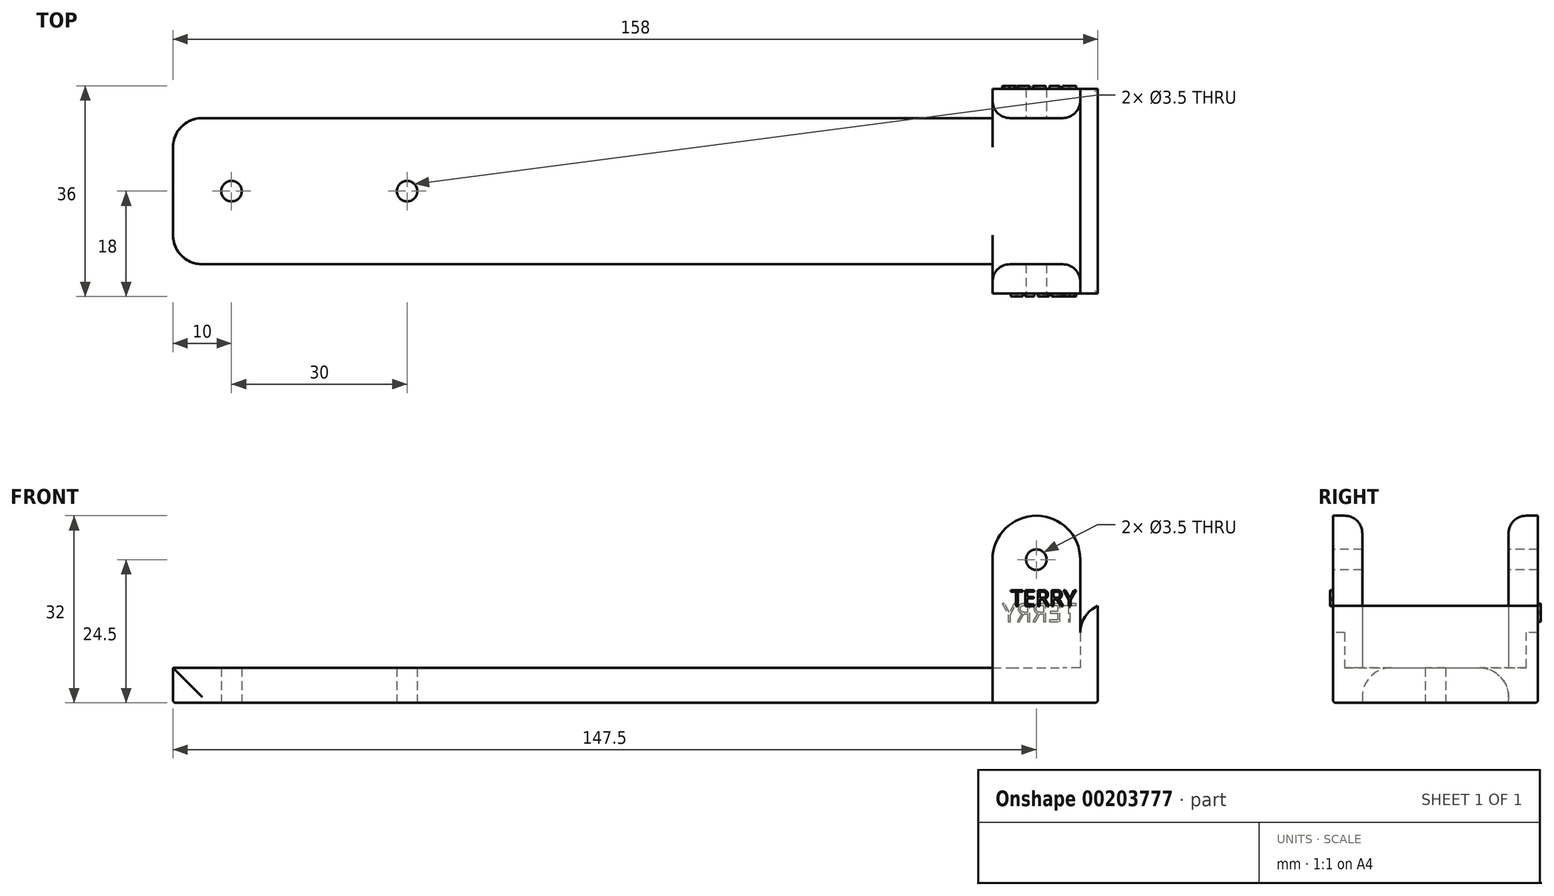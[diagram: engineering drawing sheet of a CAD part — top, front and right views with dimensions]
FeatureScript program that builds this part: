
annotation { "Feature Type Name" : "Feature", "Feature Type Description" : "" }
export const myFeature = defineFeature(function(context is Context, id is Id, definition is map)
    precondition{}
    {
        {
            var Q0;
            Q0=qCreatedBy(makeId("Top.planeOp"),FACE);
            var sketch = newSketch(context, id + "F0", { "sketchPlane" : qUnion([Q0])});
            skLineSegment(sketch, "E0.bottom", {"start": v(-77.5, -12.5) * mm, "end": v(77.5, -12.5) * mm});
            skLineSegment(sketch, "E0.top", {"start": v(-77.5, 12.5) * mm, "end": v(77.5, 12.5) * mm});
            skLineSegment(sketch, "E0.left", {"start": v(-77.5, -12.5) * mm, "end": v(-77.5, 12.5) * mm});
            skLineSegment(sketch, "E0.right", {"start": v(77.5, -12.5) * mm, "end": v(77.5, 12.5) * mm});
            skPoint(sketch, "E0.middle", {"position": v(0, 0) * mm});
            skLineSegment(sketch, "E1", {"start": v(-77.5, 0) * mm, "end": v(-67.5, 0) * mm, "construction": true});
            skPoint(sketch, "E1.endSnap0", {"position": v(-77.5, 0) * mm});
            skLineSegment(sketch, "E2", {"start": v(-67.5, 0) * mm, "end": v(-37.5, 0) * mm, "construction": true});
            skCircle(sketch, "E3", {"center": v(-67.5, 0) * mm, "radius": 1.75 * mm});
            skCircle(sketch, "E4", {"center": v(-37.5, 0) * mm, "radius": 1.75 * mm});
            skSolve(sketch);
        }
        {
            var Q0;
            Q0=makeQuery(id+"F0.imprint","IMPRINT",FACE,{"disambiguationData":[TD([[makeQuery(id+"F0.imprint","IMPRINT",EDGE,{"derivedFrom":sQuery(id+"F0.wireOp",EDGE,"E0.bottom")}),1.0]])]});
            extrude(context, id + "F1", {"entities" : qUnion([Q0]), "depth" : 6 * mm});
        }
        {
            var Q0;
            Q0=qCreatedBy(makeId("Top.planeOp"),FACE);
            var sketch = newSketch(context, id + "F2", { "sketchPlane" : qUnion([Q0])});
            skLineSegment(sketch, "E5", {"start": v(0, 0) * mm, "end": v(0, -17.5) * mm, "construction": true});
            skLineSegment(sketch, "E6", {"start": v(0, -17.5) * mm, "end": v(77.5, -17.5) * mm, "construction": true});
            skLineSegment(sketch, "E7", {"start": v(77.5, -17.5) * mm, "end": v(77.5, -12.5) * mm});
            skLineSegment(sketch, "E8", {"start": v(77.5, -12.5) * mm, "end": v(62.5, -12.5) * mm});
            skLineSegment(sketch, "E9", {"start": v(62.5, -12.5) * mm, "end": v(62.5, -17.5) * mm});
            skLineSegment(sketch, "E10", {"start": v(62.5, -17.5) * mm, "end": v(77.5, -17.5) * mm});
            skLineSegment(sketch, "E11.MirrorCS", {"start": v(62.5, 17.5) * mm, "end": v(77.5, 17.5) * mm});
            skLineSegment(sketch, "E12.MirrorCS", {"start": v(62.5, 12.5) * mm, "end": v(62.5, 17.5) * mm});
            skLineSegment(sketch, "E13.MirrorCS", {"start": v(77.5, 12.5) * mm, "end": v(62.5, 12.5) * mm});
            skLineSegment(sketch, "E14.MirrorCS", {"start": v(77.5, 17.5) * mm, "end": v(77.5, 12.5) * mm});
            skSolve(sketch);
        }
        {
            var Q0;
            Q0=makeQuery(id+"F2.imprint","IMPRINT",FACE,{"disambiguationData":[TD([[makeQuery(id+"F2.imprint","IMPRINT",EDGE,{"derivedFrom":sQuery(id+"F2.wireOp",EDGE,"E11.MirrorCS")}),-1.0]])]});
            var Q1;
            Q1=makeQuery(id+"F2.imprint","IMPRINT",FACE,{"disambiguationData":[TD([[makeQuery(id+"F2.imprint","IMPRINT",EDGE,{"derivedFrom":sQuery(id+"F2.wireOp",EDGE,"E7")}),1.0]])]});
            extrude(context, id + "F3", {"entities" : qUnion([Q0, Q1]), "operationType" : NewBodyOperationType.ADD, "depth" : 32 * mm});
        }
        {
            var Q0;
            Q0=makeQuery(id+"F3.opExtrude","SWEPT_FACE",FACE,{"disambiguationData":[OSD([sQuery(id+"F2.wireOp",EDGE,"E10")])]});
            var sketch = newSketch(context, id + "F4", { "sketchPlane" : qUnion([Q0])});
            skLineSegment(sketch, "E15", {"start": v(70, 32) * mm, "end": v(70, 24.5) * mm, "construction": true});
            skCircle(sketch, "E16", {"center": v(70, 24.5) * mm, "radius": 1.75 * mm});
            skArc(sketch, "E17", {"start": v(77.5, 24.5) * mm, "mid": v(70, 32) * mm, "end": v(62.5, 24.5) * mm});
            skLineSegment(sketch, "E18", {"start": v(70, 24.5) * mm, "end": v(46.38, 24.5) * mm, "construction": true});
            skLineSegment(sketch, "E19", {"start": v(70, 24.5) * mm, "end": v(96.72, 24.5) * mm, "construction": true});
            skLineSegment(sketch, "E20", {"start": v(62.5, 24.5) * mm, "end": v(62.5, 32) * mm});
            skLineSegment(sketch, "E21", {"start": v(62.5, 32) * mm, "end": v(70, 32) * mm});
            skLineSegment(sketch, "E22", {"start": v(77.5, 32) * mm, "end": v(77.5, 24.5) * mm});
            skSolve(sketch);
        }
        {
            var Q0;
            Q0=makeQuery(id+"F4.imprint","IMPRINT",FACE,{"disambiguationData":[TD([[makeQuery(id+"F4.imprint","IMPRINT",EDGE,{"derivedFrom":sQuery(id+"F4.wireOp",EDGE,"E16")}),1.0]])]});
            var Q1;
            {var subQ0=sQuery(id+"F4.wireOp",EDGE,"E20");Q1=makeQuery(id+"F4.imprint","IMPRINT",FACE,{"disambiguationData":[TD([[makeQuery(id+"F4.imprint","IMPRINT",EDGE,{"derivedFrom":subQ0}),1.0]])]});}
            var Q2;
            {var subQ0=sQuery(id+"F4.wireOp",EDGE,"E22");Q2=makeQuery(id+"F4.imprint","IMPRINT",FACE,{"disambiguationData":[TD([[makeQuery(id+"F4.imprint","IMPRINT",EDGE,{"derivedFrom":subQ0}),-1.0]])]});}
            extrude(context, id + "F5", {"entities" : qUnion([Q0, Q1, Q2]), "operationType" : NewBodyOperationType.REMOVE, "endBound" : BoundingType.THROUGH_ALL, "oppositeDirection" : true, "depth" : 25 * mm});
        }
        {
            var Q0;
            Q0=makeQuery(id+"F3.boolean.opBoolean","MERGE",FACE,{"derivedFrom":[makeQuery(id+"F1.opExtrude","SWEPT_FACE",FACE,{"disambiguationData":[OSD([sQuery(id+"F0.wireOp",EDGE,"E0.right")])]}),makeQuery(id+"F3.opExtrude","SWEPT_FACE",FACE,{"disambiguationData":[OSD([sQuery(id+"F2.wireOp",EDGE,"E7")])]}),makeQuery(id+"F3.opExtrude","SWEPT_FACE",FACE,{"disambiguationData":[OSD([sQuery(id+"F2.wireOp",EDGE,"E14.MirrorCS")])]})]});
            var sketch = newSketch(context, id + "F6", { "sketchPlane" : qUnion([Q0])});
            skLineSegment(sketch, "E23", {"start": v(-17.5, 0) * mm, "end": v(17.5, 0) * mm});
            skLineSegment(sketch, "E24", {"start": v(17.5, 0) * mm, "end": v(17.5, 17) * mm});
            skLineSegment(sketch, "E25", {"start": v(17.5, 17) * mm, "end": v(-17.5, 17) * mm});
            skLineSegment(sketch, "E26", {"start": v(-17.5, 17) * mm, "end": v(-17.5, 0) * mm});
            skSolve(sketch);
        }
        {
            var Q0;
            Q0=makeQuery(id+"F6.imprint","IMPRINT",FACE,{"disambiguationData":[TD([[makeQuery(id+"F6.imprint","IMPRINT",EDGE,{"derivedFrom":sQuery(id+"F6.wireOp",EDGE,"E23")}),1.0]])]});
            var Q1;
            {var subQ5=makeQuery(id+"F1.opExtrude","CAP_EDGE",EDGE,{"disambiguationData":[OSD([sQuery(id+"F0.wireOp",EDGE,"E0.right")])],"isStart":false});Q1=makeQuery(id+"F6.imprint","IMPRINT",FACE,{"disambiguationData":[TD([[makeQuery(id+"F6.imprint","IMPRINT",EDGE,{"derivedFrom":subQ5}),1.0]])]});}
            extrude(context, id + "F7", {"entities" : qUnion([Q0, Q1]), "operationType" : NewBodyOperationType.ADD, "depth" : 3 * mm});
        }
        {
            var Q0;
            Q0=makeQuery(id+"F1.opExtrude","SWEPT_EDGE",EDGE,{"disambiguationData":[OSD([sQuery(id+"F0.wireOp",EDGE,"E0.top"),sQuery(id+"F0.wireOp",EDGE,"E0.left")])]});
            var Q1;
            Q1=makeQuery(id+"F1.opExtrude","SWEPT_EDGE",EDGE,{"disambiguationData":[OSD([sQuery(id+"F0.wireOp",EDGE,"E0.bottom"),sQuery(id+"F0.wireOp",EDGE,"E0.left")])]});
            var Q2;
            {var subQ0=sQuery(id+"F0.wireOp",EDGE,"E0.right");var subQ1=sQuery(id+"F0.wireOp",EDGE,"E0.bottom");Q2=makeQuery(id+"F3.boolean.opBoolean","SPLIT",EDGE,{"disambiguationData":[TD([makeQuery(id+"F1.opExtrude","SWEPT_FACE",FACE,{"disambiguationData":[OSD([subQ0])]})])],"derivedFrom":makeQuery(id+"F1.opExtrude","CAP_EDGE",EDGE,{"disambiguationData":[OSD([subQ1])],"isStart":false})});}
            var Q3;
            {var subQ0=sQuery(id+"F0.wireOp",EDGE,"E0.right");var subQ1=sQuery(id+"F0.wireOp",EDGE,"E0.top");Q3=makeQuery(id+"F3.boolean.opBoolean","SPLIT",EDGE,{"disambiguationData":[TD([makeQuery(id+"F1.opExtrude","SWEPT_FACE",FACE,{"disambiguationData":[OSD([subQ0])]})])],"derivedFrom":makeQuery(id+"F1.opExtrude","CAP_EDGE",EDGE,{"disambiguationData":[OSD([subQ1])],"isStart":false})});}
            var Q4;
            Q4=makeQuery(id+"F1.opExtrude","CAP_EDGE",EDGE,{"disambiguationData":[OSD([sQuery(id+"F0.wireOp",EDGE,"E0.right")])],"isStart":false});
            var Q5;
            {var subQ0=sQuery(id+"F6.wireOp",EDGE,"E26");var subQ1=sQuery(id+"F6.wireOp",EDGE,"E25");Q5=makeQuery(id+"F7.boolean.opBoolean","SPLIT",EDGE,{"disambiguationData":[TD([makeQuery(id+"F1.opExtrude","SWEPT_FACE",FACE,{"disambiguationData":[OSD([sQuery(id+"F0.wireOp",EDGE,"E0.right")])]}),makeQuery(id+"F3.opExtrude","SWEPT_FACE",FACE,{"disambiguationData":[OSD([sQuery(id+"F2.wireOp",EDGE,"E7")])]}),makeQuery(id+"F3.opExtrude","SWEPT_FACE",FACE,{"disambiguationData":[OSD([sQuery(id+"F2.wireOp",EDGE,"E8")])]}),makeQuery(id+"F3.opExtrude","SWEPT_FACE",FACE,{"disambiguationData":[OSD([sQuery(id+"F2.wireOp",EDGE,"E10")])]}),makeQuery(id+"F3.opExtrude","SWEPT_FACE",FACE,{"disambiguationData":[OSD([sQuery(id+"F2.wireOp",EDGE,"E14.MirrorCS")])]}),makeQuery(id+"F7.opExtrude","CAP_FACE",FACE,{"disambiguationData":[OSD([sQuery(id+"F6.wireOp",EDGE,"E23"),sQuery(id+"F6.wireOp",EDGE,"E24"),subQ1,subQ0])],"isStart":true}),makeQuery(id+"F7.opExtrude","SWEPT_FACE",FACE,{"disambiguationData":[OSD([subQ1])]}),makeQuery(id+"F7.opExtrude","SWEPT_FACE",FACE,{"disambiguationData":[OSD([subQ0])]})])],"derivedFrom":makeQuery(id+"F7.opExtrude","CAP_EDGE",EDGE,{"disambiguationData":[OSD([subQ1])],"isStart":true})});}
            var Q6;
            {var subQ0=sQuery(id+"F6.wireOp",EDGE,"E25");var subQ1=sQuery(id+"F6.wireOp",EDGE,"E24");Q6=makeQuery(id+"F7.boolean.opBoolean","SPLIT",EDGE,{"disambiguationData":[TD([makeQuery(id+"F1.opExtrude","SWEPT_FACE",FACE,{"disambiguationData":[OSD([sQuery(id+"F0.wireOp",EDGE,"E0.right")])]}),makeQuery(id+"F3.opExtrude","SWEPT_FACE",FACE,{"disambiguationData":[OSD([sQuery(id+"F2.wireOp",EDGE,"E7")])]}),makeQuery(id+"F3.opExtrude","SWEPT_FACE",FACE,{"disambiguationData":[OSD([sQuery(id+"F2.wireOp",EDGE,"E11.MirrorCS")])]}),makeQuery(id+"F3.opExtrude","SWEPT_FACE",FACE,{"disambiguationData":[OSD([sQuery(id+"F2.wireOp",EDGE,"E13.MirrorCS")])]}),makeQuery(id+"F3.opExtrude","SWEPT_FACE",FACE,{"disambiguationData":[OSD([sQuery(id+"F2.wireOp",EDGE,"E14.MirrorCS")])]}),makeQuery(id+"F7.opExtrude","CAP_FACE",FACE,{"disambiguationData":[OSD([sQuery(id+"F6.wireOp",EDGE,"E23"),subQ1,subQ0,sQuery(id+"F6.wireOp",EDGE,"E26")])],"isStart":true}),makeQuery(id+"F7.opExtrude","SWEPT_FACE",FACE,{"disambiguationData":[OSD([subQ1])]}),makeQuery(id+"F7.opExtrude","SWEPT_FACE",FACE,{"disambiguationData":[OSD([subQ0])]})])],"derivedFrom":makeQuery(id+"F7.opExtrude","CAP_EDGE",EDGE,{"disambiguationData":[OSD([subQ0])],"isStart":true})});}
            fillet(context, id + "F8", {"entities" : qUnion([Q0, Q1, Q2, Q3, Q4, Q5, Q6]), "radius" : 5 * mm, "tangentPropagation" : true, "allowEdgeOverflow" : false});
        }
        {
            var Q0;
            {var subQ6=sQuery(id+"F2.wireOp",EDGE,"E9");var subQ7=sQuery(id+"F2.wireOp",EDGE,"E8");Q0=makeQuery(id+"F3.boolean.opBoolean","SPLIT",EDGE,{"disambiguationData":[TD([makeQuery(id+"F3.opExtrude","CAP_FACE",FACE,{"disambiguationData":[OSD([sQuery(id+"F2.wireOp",EDGE,"E7"),subQ7,subQ6,sQuery(id+"F2.wireOp",EDGE,"E10")])],"isStart":true})])],"derivedFrom":makeQuery(id+"F3.opExtrude","SWEPT_EDGE",EDGE,{"disambiguationData":[OSD([subQ7,subQ6])]})});}
            var Q1;
            {var subQ1=sQuery(id+"F2.wireOp",EDGE,"E12.MirrorCS");var subQ7=sQuery(id+"F2.wireOp",EDGE,"E13.MirrorCS");Q1=makeQuery(id+"F3.boolean.opBoolean","SPLIT",EDGE,{"disambiguationData":[TD([makeQuery(id+"F3.opExtrude","CAP_FACE",FACE,{"disambiguationData":[OSD([sQuery(id+"F2.wireOp",EDGE,"E7"),sQuery(id+"F2.wireOp",EDGE,"E8"),sQuery(id+"F2.wireOp",EDGE,"E9"),sQuery(id+"F2.wireOp",EDGE,"E10")])],"isStart":true})])],"derivedFrom":makeQuery(id+"F3.opExtrude","SWEPT_EDGE",EDGE,{"disambiguationData":[OSD([subQ1,subQ7])]})});}
            fillet(context, id + "F9", {"entities" : qUnion([Q0, Q1]), "radius" : 3 * mm, "tangentPropagation" : true, "allowEdgeOverflow" : false});
        }
        {
            var Q0;
            {var subQ0=sQuery(id+"F0.wireOp",EDGE,"E0.left");var subQ1=sQuery(id+"F0.wireOp",EDGE,"E0.bottom");Q0=makeQuery(id+"F3.boolean.opBoolean","SPLIT",EDGE,{"disambiguationData":[TD([makeQuery(id+"F1.opExtrude","SWEPT_FACE",FACE,{"disambiguationData":[OSD([subQ0])]})])],"derivedFrom":makeQuery(id+"F1.opExtrude","CAP_EDGE",EDGE,{"disambiguationData":[OSD([subQ1])],"isStart":false})});}
            var Q1;
            Q1=makeQuery(id+"F1.opExtrude","CAP_EDGE",EDGE,{"disambiguationData":[OSD([sQuery(id+"F0.wireOp",EDGE,"E0.top")])],"isStart":true});
            var Q2;
            Q2=makeQuery(id+"F7.opExtrude","CAP_EDGE",EDGE,{"disambiguationData":[OSD([sQuery(id+"F6.wireOp",EDGE,"E23")])],"isStart":false});
            var Q3;
            Q3=makeQuery(id+"F7.boolean.opBoolean","MERGE",EDGE,{"derivedFrom":[makeQuery(id+"F3.opExtrude","CAP_EDGE",EDGE,{"disambiguationData":[OSD([sQuery(id+"F2.wireOp",EDGE,"E10")])],"isStart":true}),makeQuery(id+"F7.opExtrude","SWEPT_EDGE",EDGE,{"disambiguationData":[OSD([sQuery(id+"F6.wireOp",EDGE,"E23"),sQuery(id+"F6.wireOp",EDGE,"E26")])]})]});
            var Q4;
            Q4=makeQuery(id+"F7.boolean.opBoolean","MERGE",EDGE,{"derivedFrom":[makeQuery(id+"F3.opExtrude","CAP_EDGE",EDGE,{"disambiguationData":[OSD([sQuery(id+"F2.wireOp",EDGE,"E11.MirrorCS")])],"isStart":true}),makeQuery(id+"F7.opExtrude","SWEPT_EDGE",EDGE,{"disambiguationData":[OSD([sQuery(id+"F6.wireOp",EDGE,"E23"),sQuery(id+"F6.wireOp",EDGE,"E24")])]})]});
            var Q5;
            {var subQ0=sQuery(id+"F2.wireOp",EDGE,"E13.MirrorCS");var subQ1=sQuery(id+"F2.wireOp",EDGE,"E12.MirrorCS");var subQ2=makeQuery(id+"F3.opExtrude","CAP_FACE",FACE,{"disambiguationData":[OSD([sQuery(id+"F2.wireOp",EDGE,"E11.MirrorCS"),subQ1,subQ0,sQuery(id+"F2.wireOp",EDGE,"E14.MirrorCS")])],"isStart":true});var subQ3=makeQuery(id+"F3.opExtrude","CAP_FACE",FACE,{"disambiguationData":[OSD([sQuery(id+"F2.wireOp",EDGE,"E7"),sQuery(id+"F2.wireOp",EDGE,"E8"),sQuery(id+"F2.wireOp",EDGE,"E9"),sQuery(id+"F2.wireOp",EDGE,"E10")])],"isStart":true});var subQ4=sQuery(id+"F0.wireOp",EDGE,"E4");var subQ5=sQuery(id+"F0.wireOp",EDGE,"E3");var subQ6=sQuery(id+"F0.wireOp",EDGE,"E0.right");var subQ7=sQuery(id+"F0.wireOp",EDGE,"E0.left");var subQ8=sQuery(id+"F0.wireOp",EDGE,"E0.top");var subQ9=sQuery(id+"F0.wireOp",EDGE,"E0.bottom");var subQ10=makeQuery(id+"F1.opExtrude","CAP_FACE",FACE,{"disambiguationData":[OSD([subQ9,subQ8,subQ7,subQ6,subQ5,subQ4])],"isStart":true});Q5=makeQuery(id+"F9.opFillet","BLEND_EDGE",EDGE,{"blendedFrom":[makeQuery(id+"F3.boolean.opBoolean","SPLIT",EDGE,{"disambiguationData":[TD([subQ3])],"derivedFrom":makeQuery(id+"F3.opExtrude","SWEPT_EDGE",EDGE,{"disambiguationData":[OSD([subQ1,subQ0])]})}),makeQuery(id+"F7.boolean.opBoolean","MERGE",FACE,{"derivedFrom":[makeQuery(id+"F3.boolean.opBoolean","MERGE",FACE,{"derivedFrom":[subQ10,subQ3,subQ2]}),makeQuery(id+"F7.opExtrude","SWEPT_FACE",FACE,{"disambiguationData":[OSD([sQuery(id+"F6.wireOp",EDGE,"E23")])]})]})],"blendedInto":[makeQuery(id+"F7.boolean.opBoolean","MERGE",FACE,{"derivedFrom":[makeQuery(id+"F3.boolean.opBoolean","MERGE",FACE,{"derivedFrom":[subQ10,subQ3,subQ2]}),makeQuery(id+"F7.opExtrude","SWEPT_FACE",FACE,{"disambiguationData":[OSD([sQuery(id+"F6.wireOp",EDGE,"E23")])]})]})]});}
            var Q6;
            {var subQ0=makeQuery(id+"F3.opExtrude","CAP_FACE",FACE,{"disambiguationData":[OSD([sQuery(id+"F2.wireOp",EDGE,"E11.MirrorCS"),sQuery(id+"F2.wireOp",EDGE,"E12.MirrorCS"),sQuery(id+"F2.wireOp",EDGE,"E13.MirrorCS"),sQuery(id+"F2.wireOp",EDGE,"E14.MirrorCS")])],"isStart":true});var subQ1=sQuery(id+"F2.wireOp",EDGE,"E9");var subQ2=sQuery(id+"F2.wireOp",EDGE,"E8");var subQ3=makeQuery(id+"F3.opExtrude","CAP_FACE",FACE,{"disambiguationData":[OSD([sQuery(id+"F2.wireOp",EDGE,"E7"),subQ2,subQ1,sQuery(id+"F2.wireOp",EDGE,"E10")])],"isStart":true});var subQ4=sQuery(id+"F0.wireOp",EDGE,"E4");var subQ5=sQuery(id+"F0.wireOp",EDGE,"E3");var subQ6=sQuery(id+"F0.wireOp",EDGE,"E0.right");var subQ7=sQuery(id+"F0.wireOp",EDGE,"E0.left");var subQ8=sQuery(id+"F0.wireOp",EDGE,"E0.top");var subQ9=sQuery(id+"F0.wireOp",EDGE,"E0.bottom");var subQ10=makeQuery(id+"F1.opExtrude","CAP_FACE",FACE,{"disambiguationData":[OSD([subQ9,subQ8,subQ7,subQ6,subQ5,subQ4])],"isStart":true});Q6=makeQuery(id+"F9.opFillet","BLEND_EDGE",EDGE,{"blendedFrom":[makeQuery(id+"F3.boolean.opBoolean","SPLIT",EDGE,{"disambiguationData":[TD([subQ3])],"derivedFrom":makeQuery(id+"F3.opExtrude","SWEPT_EDGE",EDGE,{"disambiguationData":[OSD([subQ2,subQ1])]})}),makeQuery(id+"F7.boolean.opBoolean","MERGE",FACE,{"derivedFrom":[makeQuery(id+"F3.boolean.opBoolean","MERGE",FACE,{"derivedFrom":[subQ10,subQ3,subQ0]}),makeQuery(id+"F7.opExtrude","SWEPT_FACE",FACE,{"disambiguationData":[OSD([sQuery(id+"F6.wireOp",EDGE,"E23")])]})]})],"blendedInto":[makeQuery(id+"F7.boolean.opBoolean","MERGE",FACE,{"derivedFrom":[makeQuery(id+"F3.boolean.opBoolean","MERGE",FACE,{"derivedFrom":[subQ10,subQ3,subQ0]}),makeQuery(id+"F7.opExtrude","SWEPT_FACE",FACE,{"disambiguationData":[OSD([sQuery(id+"F6.wireOp",EDGE,"E23")])]})]})]});}
            fillet(context, id + "F10", {"entities" : qUnion([Q0, Q1, Q2, Q3, Q4, Q5, Q6]), "radius" : 0.5 * mm, "tangentPropagation" : true, "allowEdgeOverflow" : false});
        }
        {
            var Q0;
            Q0=makeQuery(id+"F7.boolean.opBoolean","MERGE",FACE,{"derivedFrom":[makeQuery(id+"F3.opExtrude","SWEPT_FACE",FACE,{"disambiguationData":[OSD([sQuery(id+"F2.wireOp",EDGE,"E10")])]}),makeQuery(id+"F7.opExtrude","SWEPT_FACE",FACE,{"disambiguationData":[OSD([sQuery(id+"F6.wireOp",EDGE,"E26")])]})]});
            var sketch = newSketch(context, id + "F11", { "sketchPlane" : qUnion([Q0])});
            skText(sketch, "E27", { "text": "TERRY", "fontName": "OpenSans-Regular.ttf"});
            const initialGuessF11  = {"E27": [0.0656, 0.01655, 1, 0, 0.00277]};
            skSetInitialGuess(sketch, initialGuessF11);
            skSolve(sketch);
        }
        {
            var Q0;
            Q0 = qSketchRegion(id + "F11", true);
            extrude(context, id + "F12", {"entities" : qUnion([Q0]), "operationType" : NewBodyOperationType.ADD, "depth" : 0.5 * mm});
        }
        {
            var Q0;
            Q0=makeQuery(id+"F7.boolean.opBoolean","MERGE",FACE,{"derivedFrom":[makeQuery(id+"F3.opExtrude","SWEPT_FACE",FACE,{"disambiguationData":[OSD([sQuery(id+"F2.wireOp",EDGE,"E11.MirrorCS")])]}),makeQuery(id+"F7.opExtrude","SWEPT_FACE",FACE,{"disambiguationData":[OSD([sQuery(id+"F6.wireOp",EDGE,"E24")])]})]});
            var sketch = newSketch(context, id + "F13", { "sketchPlane" : qUnion([Q0])});
            skText(sketch, "E28", { "text": "TERRY", "fontName": "OpenSans-Regular.ttf"});
            const initialGuessF13  = {"E28": [-0.07684, 0.01388, 1, 0, 0.00314]};
            skSetInitialGuess(sketch, initialGuessF13);
            skSolve(sketch);
        }
        {
            var Q0;
            Q0 = qSketchRegion(id + "F13", true);
            extrude(context, id + "F14", {"entities" : qUnion([Q0]), "operationType" : NewBodyOperationType.ADD, "depth" : 0.5 * mm});
        }
    });
